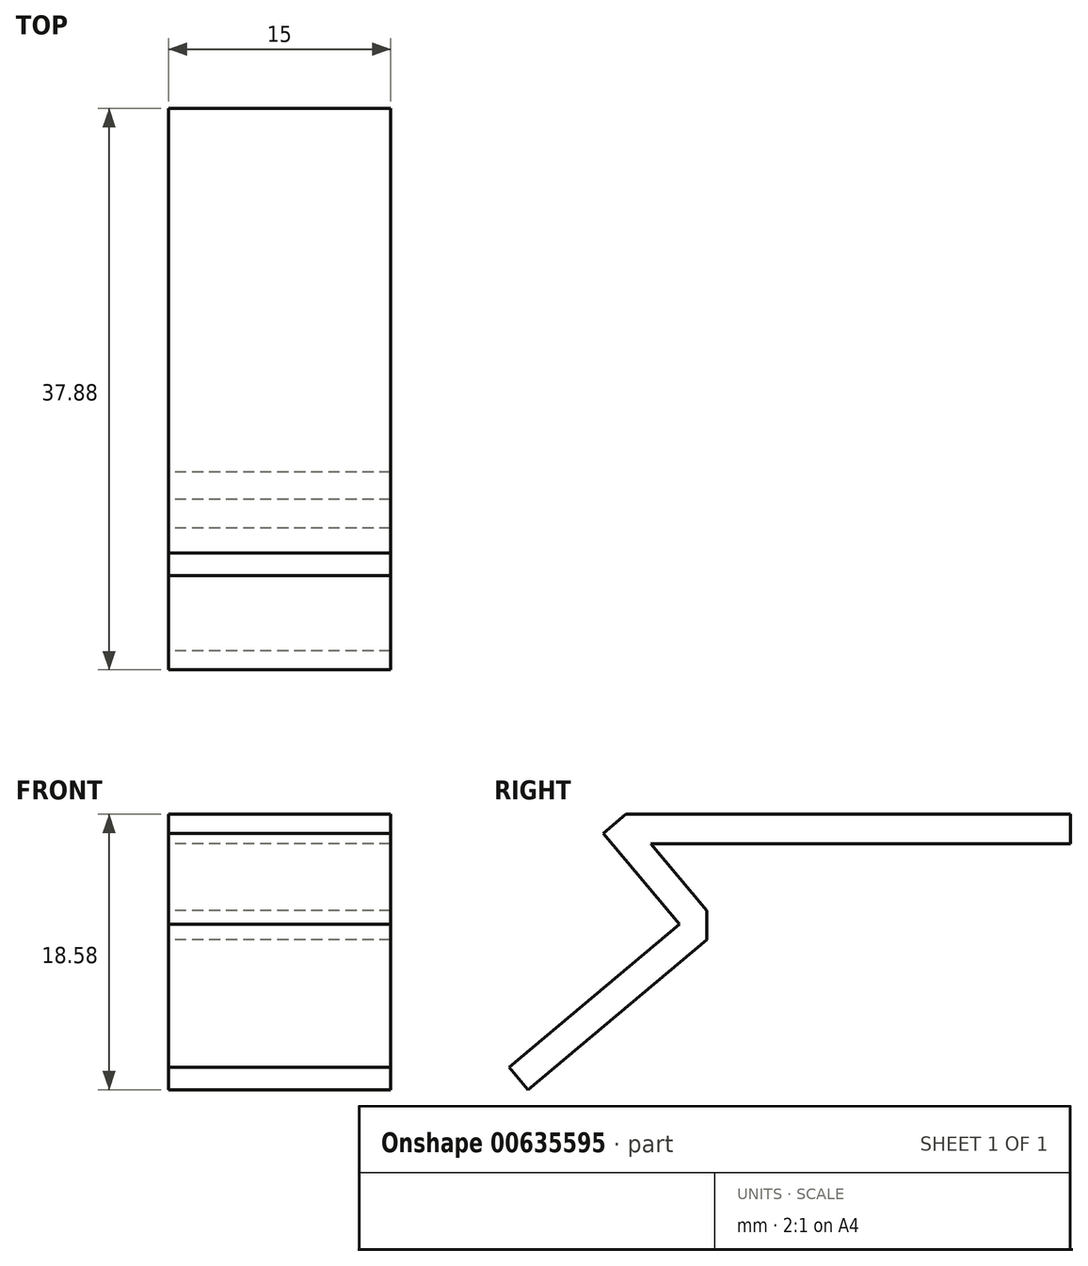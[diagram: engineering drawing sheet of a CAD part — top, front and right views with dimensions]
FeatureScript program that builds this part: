
annotation { "Feature Type Name" : "Feature", "Feature Type Description" : "" }
export const myFeature = defineFeature(function(context is Context, id is Id, definition is map)
    precondition{}
    {
        {
            var Q0;
            Q0=qCreatedBy(makeId("Right.planeOp"),FACE);
            var sketch = newSketch(context, id + "F0", { "sketchPlane" : qUnion([Q0])});
            skLineSegment(sketch, "E0", {"start": v(-29.58, -12.11) * mm, "end": v(-17.53, -2) * mm});
            skLineSegment(sketch, "E1", {"start": v(-17.53, -0.03) * mm, "end": v(-21.31, 4.47) * mm});
            skLineSegment(sketch, "E2", {"start": v(-23, 6.47) * mm, "end": v(-24.52, 5.19) * mm});
            skLineSegment(sketch, "E3", {"start": v(-24.52, 5.19) * mm, "end": v(-19.38, -0.94) * mm});
            skLineSegment(sketch, "E4", {"start": v(-19.38, -0.94) * mm, "end": v(-30.87, -10.58) * mm});
            skLineSegment(sketch, "E5", {"start": v(-30.87, -10.58) * mm, "end": v(-29.58, -12.11) * mm});
            skLineSegment(sketch, "E6.bottom", {"start": v(-23, 6.47) * mm, "end": v(7, 6.47) * mm});
            skLineSegment(sketch, "E6.top", {"start": v(-21.31, 4.47) * mm, "end": v(7, 4.47) * mm});
            skLineSegment(sketch, "E6.right", {"start": v(7, 6.47) * mm, "end": v(7, 4.47) * mm});
            skLineSegment(sketch, "E7", {"start": v(-17.53, -2) * mm, "end": v(-17.53, -0.03) * mm});
            skSolve(sketch);
        }
        {
            var Q0;
            Q0=makeQuery(id+"F0.imprint","IMPRINT",FACE,{"disambiguationData":[TD([[makeQuery(id+"F0.imprint","IMPRINT",EDGE,{"derivedFrom":sQuery(id+"F0.wireOp",EDGE,"E0")}),1.0]])]});
            extrude(context, id + "F1", {"entities" : qUnion([Q0]), "depth" : 15 * mm, "offsetDistance" : 25 * mm});
        }
    });
